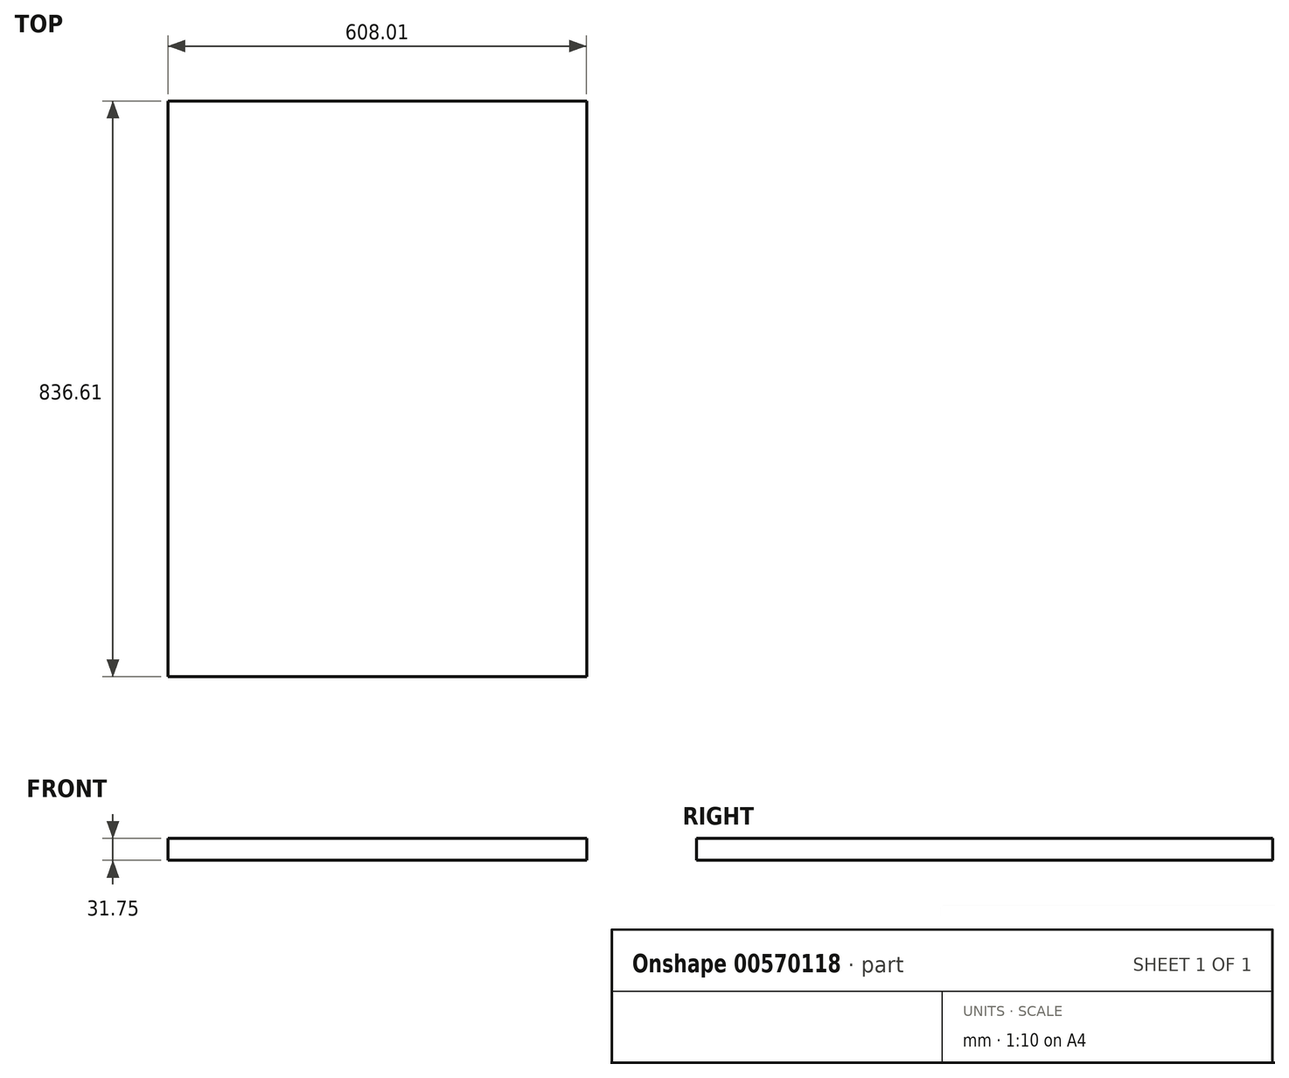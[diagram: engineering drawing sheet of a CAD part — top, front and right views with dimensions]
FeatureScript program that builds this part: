
annotation { "Feature Type Name" : "Feature", "Feature Type Description" : "" }
export const myFeature = defineFeature(function(context is Context, id is Id, definition is map)
    precondition{}
    {
        {
            var Q0;
            Q0=qCreatedBy(makeId("Front.planeOp"),FACE);
            var sketch = newSketch(context, id + "F0", { "sketchPlane" : qUnion([Q0])});
            skLineSegment(sketch, "E0.bottom", {"start": v(0, 0) * mm, "end": v(608.01, 0) * mm});
            skLineSegment(sketch, "E0.top", {"start": v(0, -31.75) * mm, "end": v(608.01, -31.75) * mm});
            skLineSegment(sketch, "E0.left", {"start": v(0, 0) * mm, "end": v(0, -31.75) * mm});
            skLineSegment(sketch, "E0.right", {"start": v(608.01, 0) * mm, "end": v(608.01, -31.75) * mm});
            skSolve(sketch);
        }
        {
            var Q0;
            Q0 = qSketchRegion(id + "F0", true);
            extrude(context, id + "F1", {"entities" : qUnion([Q0]), "depth" : 836.6 * mm, "offsetDistance" : 25.4 * mm});
        }
    });
